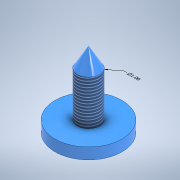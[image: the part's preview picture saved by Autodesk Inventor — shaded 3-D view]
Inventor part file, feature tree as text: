
AUTODESK INVENTOR PART (.ipt)
format: ipt  version: 2021.1 (Build 251245000, 245)  size: 123,392 bytes
history: native  units: in
note: dims shown in document units (in); Inventor stores cm internally (conversion verified against a paired STEP export)
features: other x2, revolve x1, thread x1, sketch x1
ambient origin geometry x8: Origin, YZ Plane, XZ Plane, XY Plane, X Axis, Y Axis, Z Axis, Center Point
bodies: Solid1 (feature_tree)
feature tree (5):
  other  "Annotations"
  revolve  "Revolution1"  [1 undecoded]
  thread  "Thread1"  [1 undecoded]
  sketch  "Sketch1"  dims[d1=0.0in d2=0.5in d5=30.0deg d7=0.5in d9=90.0deg d10=4.134in d11=0.0in d14=2.0in d12=0.2536in d13=1.0in]
  other  "Diameter Dimension 1"
note: 2 required parameter values undecoded (feature->parameter linkage not recoverable at this tier; creation-order binding heuristic only, values carry confidence <= 0.55)